# Revit family: Mailboxes_4C-Salsbury_Industries-Rear_Load-14_Door_High_Units
name_source: partatom
category: Specialty Equipment
revit_build: Autodesk Revit 2016 (Build: 20150714_1515(x64)
units: mm (PartAtom-declared; Revit-internal decimal feet)

## family parameters
Always vertical = Yes
Cut with Voids When Loaded = No
Host = Wall
OmniClass Number = 23.40.90.14.11
OmniClass Title = Mail Boxes
Part Type = Normal
Room Calculation Point = No
Round Connector Dimension = Use Diameter
Shared = No

## types (14) — shared parameters
Assembly Code = C1030910
Assembly Description = Mailboxes
Back Enclosure Material = Aluminum - Salsbury Finish - Anodized
Bottom Back Plate = No
Depth = 17.025"
Height = 51.500"
Latch Distance = 9.515"
Latch Locks-Right Side = Yes
Lock Material = Stainless Steel - Salsbury Finish -  Polished
Manufacturer = Salsbury Industries
MasterFormat Number = 10 55 00
MasterFormat Title = Postal Specialties
OmniClass 23 Number = 23.40.90.14.11
OmniClass 23 Title = Mail Boxes
Top Back Plate = No
URL = www.mailboxes.com
Version = 3.0 (06/30/17)

## per-type parameters (varying)
- 3714D-16 RL: Description=14 Door High Unit:  16 MB1, 2 PL5, OM2; Door Slot L1=3700 Series 4C Door Configurations : MB1 Door; Door Slot L10=3700 Series 4C Door Configurations : Empty; Door Slot L11=3700 Series 4C Door Configurations : Empty; Door Slot L12=3700 Series 4C Door Configurations : Empty; Door Slot L13=3700 Series 4C Door Configurations : Empty; Door Slot L14=3700 Series 4C Parcel Configurations : PL5 w/ Divider; Door Slot L2=3700 Series 4C Door Configurations : MB1 Door w/ Divider; Door Slot L3=3700 Series 4C Door Configurations : MB1 Door w/ Divider; Door Slot L4=3700 Series 4C Door Configurations : MB1 Door w/ Divider; Door Slot L5=3700 Series 4C Door Configurations : MB1 Door w/ Divider; Door Slot L6=3700 Series 4C Door Configurations : MB1 Door w/ Divider; Door Slot L7=3700 Series 4C Door Configurations : MB1 Door w/ Divider; Door Slot L8=3700 Series 4C Door Configurations : MB1 Door w/ Divider; Door Slot L9=3700 Series 4C Door Configurations : MB1 Door w/ Divider; Door Slot R1=3700 Series 4C Door Configurations : MB1 Door w/ Divider; Door Slot R10=3700 Series 4C Door Configurations : Empty; Door Slot R11=3700 Series 4C Door Configurations : Empty; Door Slot R12=3700 Series 4C Door Configurations : Empty; Door Slot R13=3700 Series 4C Door Configurations : Empty; Door Slot R14=3700 Series 4C Parcel Configurations : PL5 w/ Divider; Door Slot R2=3700 Series 4C Door Configurations : MB1 Door w/ Divider; Door Slot R3=3700 Series 4C Door Configurations : MB1 Door w/ Divider; Door Slot R4=3700 Series 4C Door Configurations : MB1 Door w/ Divider; Door Slot R5=3700 Series 4C Door Configurations : MB1 Door w/ Divider; Door Slot R6=3700 Series 4C Door Configurations : Empty; Door Slot R7=3700 Series 4C OM2 Configuration : OM2-RL; Door Slot R8=3700 Series 4C Door Configurations : MB1 Door w/ Divider; Door Slot R9=3700 Series 4C Door Configurations : MB1 Door w/ Divider; Latch Alignment=14.857"; Latch Locks-Left Side=Yes; Left Inside Wall=Yes; Right Inside Wall=Yes; Type Comments=4C Standard Horizontal Mailbox - Rear Loading; Vertical Center Divider=Yes; Width=31.098"
- 3714S-2B RL: Description=14 Door High Unit:- 2 Receptacle Bins; Door Slot L1=3700 Series 4C Door Configurations : Empty; Door Slot L10=3700 Series 4C Door Configurations : Empty; Door Slot L11=3700 Series 4C Door Configurations : Empty; Door Slot L12=3700 Series 4C Door Configurations : Empty; Door Slot L13=3700 Series 4C Door Configurations : Empty; Door Slot L14=3700 Series 4C Door Configurations : Empty; Door Slot L2=3700 Series 4C Door Configurations : Empty; Door Slot L3=3700 Series 4C Door Configurations : Empty; Door Slot L4=3700 Series 4C Door Configurations : Empty; Door Slot L5=3700 Series 4C Door Configurations : Empty; Door Slot L6=3700 Series 4C Door Configurations : Empty; Door Slot L7=3700 Series 4C Door Configurations : Empty; Door Slot L8=3700 Series 4C Door Configurations : Empty; Door Slot L9=3700 Series 4C Door Configurations : Empty; Door Slot R1=3700 Series 4C Door Configurations : Empty; Door Slot R10=3700 Series 4C Door Configurations : Empty; Door Slot R11=3700 Series 4C Door Configurations : Empty; Door Slot R12=3700 Series 4C Door Configurations : Empty; Door Slot R13=3700 Series 4C Door Configurations : Empty; Door Slot R14=4C-14 Door High Receptacle; Door Slot R2=3700 Series 4C Door Configurations : Empty; Door Slot R3=3700 Series 4C Door Configurations : Empty; Door Slot R4=3700 Series 4C Door Configurations : Empty; Door Slot R5=3700 Series 4C Door Configurations : Empty; Door Slot R6=3700 Series 4C Door Configurations : Empty; Door Slot R7=3700 Series 4C Door Configurations : Empty; Door Slot R8=3700 Series 4C Door Configurations : Empty; Door Slot R9=3700 Series 4C Door Configurations : Empty; Latch Alignment=13.876"; Latch Locks-Left Side=No; Left Inside Wall=No; Right Inside Wall=No; Type Comments=4C Horizontal Receptacle Bin - Rear Loading; Vertical Center Divider=No; Width=16.344"
- 3714S-07 RL: Description=14 Door High Unit:  7 MB1, 1 PL5, OM2; Door Slot L1=3700 Series 4C Door Configurations : Empty; Door Slot L10=3700 Series 4C Door Configurations : Empty; Door Slot L11=3700 Series 4C Door Configurations : Empty; Door Slot L12=3700 Series 4C Door Configurations : Empty; Door Slot L13=3700 Series 4C Door Configurations : Empty; Door Slot L14=3700 Series 4C Door Configurations : Empty; Door Slot L2=3700 Series 4C Door Configurations : Empty; Door Slot L3=3700 Series 4C Door Configurations : Empty; Door Slot L4=3700 Series 4C Door Configurations : Empty; Door Slot L5=3700 Series 4C Door Configurations : Empty; Door Slot L6=3700 Series 4C Door Configurations : Empty; Door Slot L7=3700 Series 4C Door Configurations : Empty; Door Slot L8=3700 Series 4C Door Configurations : Empty; Door Slot L9=3700 Series 4C Door Configurations : Empty; Door Slot R1=3700 Series 4C Door Configurations : MB1 Door; Door Slot R10=3700 Series 4C Door Configurations : Empty; Door Slot R11=3700 Series 4C Door Configurations : Empty; Door Slot R12=3700 Series 4C Door Configurations : Empty; Door Slot R13=3700 Series 4C Door Configurations : Empty; Door Slot R14=3700 Series 4C Parcel Configurations : PL5 w/ Divider; Door Slot R2=3700 Series 4C Door Configurations : MB1 Door w/ Divider; Door Slot R3=3700 Series 4C Door Configurations : MB1 Door w/ Divider; Door Slot R4=3700 Series 4C Door Configurations : MB1 Door w/ Divider; Door Slot R5=3700 Series 4C Door Configurations : MB1 Door w/ Divider; Door Slot R6=3700 Series 4C Door Configurations : Empty; Door Slot R7=3700 Series 4C OM2 Configuration : OM2-RL; Door Slot R8=3700 Series 4C Door Configurations : MB1 Door w/ Divider; Door Slot R9=3700 Series 4C Door Configurations : MB1 Door w/ Divider; Latch Alignment=13.876"; Latch Locks-Left Side=No; Left Inside Wall=No; Right Inside Wall=No; Type Comments=4C Standard Horizontal Mailbox - Rear Loading; Vertical Center Divider=No; Width=16.344"
- 3714S-1C RL: Description=14 Door High Unit; Door Slot L1=3700 Series 4C Door Configurations : Empty; Door Slot L10=3700 Series 4C Door Configurations : Empty; Door Slot L11=3700 Series 4C Door Configurations : Empty; Door Slot L12=3700 Series 4C Door Configurations : Empty; Door Slot L13=3700 Series 4C Door Configurations : Empty; Door Slot L14=3700 Series 4C Door Configurations : Empty; Door Slot L2=3700 Series 4C Door Configurations : Empty; Door Slot L3=3700 Series 4C Door Configurations : Empty; Door Slot L4=3700 Series 4C Door Configurations : Empty; Door Slot L5=3700 Series 4C Door Configurations : Empty; Door Slot L6=3700 Series 4C Door Configurations : Empty; Door Slot L7=3700 Series 4C Door Configurations : Empty; Door Slot L8=3700 Series 4C Door Configurations : Empty; Door Slot L9=3700 Series 4C Door Configurations : Empty; Door Slot R1=3700 Series 4C Door Configurations : Empty; Door Slot R10=3700 Series 4C Door Configurations : Empty; Door Slot R11=3700 Series 4C Door Configurations : Empty; Door Slot R12=3700 Series 4C Door Configurations : Empty; Door Slot R13=3700 Series 4C Door Configurations : Empty; Door Slot R14=4C-14 Door High Collection Box; Door Slot R2=3700 Series 4C Door Configurations : Empty; Door Slot R3=3700 Series 4C Door Configurations : Empty; Door Slot R4=3700 Series 4C Door Configurations : Empty; Door Slot R5=3700 Series 4C Door Configurations : Empty; Door Slot R6=3700 Series 4C Door Configurations : Empty; Door Slot R7=3700 Series 4C Door Configurations : Empty; Door Slot R8=3700 Series 4C Door Configurations : Empty; Door Slot R9=3700 Series 4C Door Configurations : Empty; Latch Alignment=13.876"; Latch Locks-Left Side=No; Left Inside Wall=No; Right Inside Wall=No; Type Comments=4C Horizontal Collection Box - Rear Loading; Vertical Center Divider=No; Width=16.344"
- 3714D-15 RL: Description=14 Door High Unit:  15 MB1, 1 PL5, 1 PL6, OM2; Door Slot L1=3700 Series 4C Door Configurations : MB1 Door; Door Slot L10=3700 Series 4C Door Configurations : Empty; Door Slot L11=3700 Series 4C Door Configurations : Empty; Door Slot L12=3700 Series 4C Door Configurations : Empty; Door Slot L13=3700 Series 4C Door Configurations : Empty; Door Slot L14=3700 Series 4C Parcel Configurations : PL6 w/ Divider; Door Slot L2=3700 Series 4C Door Configurations : MB1 Door w/ Divider; Door Slot L3=3700 Series 4C Door Configurations : MB1 Door w/ Divider; Door Slot L4=3700 Series 4C Door Configurations : MB1 Door w/ Divider; Door Slot L5=3700 Series 4C Door Configurations : MB1 Door w/ Divider; Door Slot L6=3700 Series 4C Door Configurations : MB1 Door w/ Divider; Door Slot L7=3700 Series 4C Door Configurations : MB1 Door w/ Divider; Door Slot L8=3700 Series 4C Door Configurations : MB1 Door w/ Divider; Door Slot L9=3700 Series 4C Door Configurations : Empty; Door Slot R1=3700 Series 4C Door Configurations : MB1 Door w/ Divider; Door Slot R10=3700 Series 4C Door Configurations : Empty; Door Slot R11=3700 Series 4C Door Configurations : Empty; Door Slot R12=3700 Series 4C Door Configurations : Empty; Door Slot R13=3700 Series 4C Door Configurations : Empty; Door Slot R14=3700 Series 4C Parcel Configurations : PL5 w/ Divider; Door Slot R2=3700 Series 4C Door Configurations : MB1 Door w/ Divider; Door Slot R3=3700 Series 4C Door Configurations : MB1 Door w/ Divider; Door Slot R4=3700 Series 4C Door Configurations : MB1 Door w/ Divider; Door Slot R5=3700 Series 4C Door Configurations : MB1 Door w/ Divider; Door Slot R6=3700 Series 4C Door Configurations : Empty; Door Slot R7=3700 Series 4C OM2 Configuration : OM2-RL; Door Slot R8=3700 Series 4C Door Configurations : MB1 Door w/ Divider; Door Slot R9=3700 Series 4C Door Configurations : MB1 Door w/ Divider; Latch Alignment=14.857"; Latch Locks-Left Side=Yes; Left Inside Wall=Yes; Right Inside Wall=Yes; Type Comments=4C Standard Horizontal Mailbox - Rear Loading; Vertical Center Divider=Yes; Width=31.098"
- 3714D-14 RL: Description=14 Door High Unit:  14 MB1, 2 PL6, OM2; Door Slot L1=3700 Series 4C Door Configurations : MB1 Door; Door Slot L10=3700 Series 4C Door Configurations : Empty; Door Slot L11=3700 Series 4C Door Configurations : Empty; Door Slot L12=3700 Series 4C Door Configurations : Empty; Door Slot L13=3700 Series 4C Door Configurations : Empty; Door Slot L14=3700 Series 4C Parcel Configurations : PL6 w/ Divider; Door Slot L2=3700 Series 4C Door Configurations : MB1 Door w/ Divider; Door Slot L3=3700 Series 4C Door Configurations : MB1 Door w/ Divider; Door Slot L4=3700 Series 4C Door Configurations : MB1 Door w/ Divider; Door Slot L5=3700 Series 4C Door Configurations : MB1 Door w/ Divider; Door Slot L6=3700 Series 4C Door Configurations : MB1 Door w/ Divider; Door Slot L7=3700 Series 4C Door Configurations : MB1 Door w/ Divider; Door Slot L8=3700 Series 4C Door Configurations : MB1 Door w/ Divider; Door Slot L9=3700 Series 4C Door Configurations : Empty; Door Slot R1=3700 Series 4C Door Configurations : MB1 Door w/ Divider; Door Slot R10=3700 Series 4C Door Configurations : Empty; Door Slot R11=3700 Series 4C Door Configurations : Empty; Door Slot R12=3700 Series 4C Door Configurations : Empty; Door Slot R13=3700 Series 4C Door Configurations : Empty; Door Slot R14=3700 Series 4C Parcel Configurations : PL6 w/ Divider; Door Slot R2=3700 Series 4C Door Configurations : MB1 Door w/ Divider; Door Slot R3=3700 Series 4C Door Configurations : MB1 Door w/ Divider; Door Slot R4=3700 Series 4C Door Configurations : MB1 Door w/ Divider; Door Slot R5=3700 Series 4C Door Configurations : MB1 Door w/ Divider; Door Slot R6=3700 Series 4C Door Configurations : Empty; Door Slot R7=3700 Series 4C OM2 Configuration : OM2-RL; Door Slot R8=3700 Series 4C Door Configurations : MB1 Door w/ Divider; Door Slot R9=3700 Series 4C Door Configurations : Empty; Latch Alignment=14.857"; Latch Locks-Left Side=Yes; Left Inside Wall=Yes; Right Inside Wall=Yes; Type Comments=4C Standard Horizontal Mailbox - Rear Loading; Vertical Center Divider=Yes; Width=31.098"
- 3714D-07 RL: Description=14 Door High Unit:  7 MB2, 2 PL6, OM2; Door Slot L1=3700 Series 4C Door Configurations : Empty; Door Slot L10=3700 Series 4C Door Configurations : Empty; Door Slot L11=3700 Series 4C Door Configurations : Empty; Door Slot L12=3700 Series 4C Door Configurations : Empty; Door Slot L13=3700 Series 4C Door Configurations : Empty; Door Slot L14=3700 Series 4C Parcel Configurations : PL6 w/ Divider; Door Slot L2=3700 Series 4C Door Configurations : MB2 Door; Door Slot L3=3700 Series 4C Door Configurations : Empty; Door Slot L4=3700 Series 4C Door Configurations : MB2 Door w/ Divider; Door Slot L5=3700 Series 4C Door Configurations : Empty; Door Slot L6=3700 Series 4C Door Configurations : MB2 Door w/ Divider; Door Slot L7=3700 Series 4C Door Configurations : Empty; Door Slot L8=3700 Series 4C Door Configurations : MB2 Door w/ Divider; Door Slot L9=3700 Series 4C Door Configurations : Empty; Door Slot R1=3700 Series 4C Door Configurations : Empty; Door Slot R10=3700 Series 4C Door Configurations : Empty; Door Slot R11=3700 Series 4C Door Configurations : Empty; Door Slot R12=3700 Series 4C Door Configurations : Empty; Door Slot R13=3700 Series 4C Door Configurations : Empty; Door Slot R14=3700 Series 4C Parcel Configurations : PL6 w/ Divider; Door Slot R2=3700 Series 4C Door Configurations : MB2 Door; Door Slot R3=3700 Series 4C Door Configurations : Empty; Door Slot R4=3700 Series 4C Door Configurations : MB2 Door w/ Divider; Door Slot R5=3700 Series 4C Door Configurations : Empty; Door Slot R6=3700 Series 4C Door Configurations : MB2 Door w/ Divider; Door Slot R7=3700 Series 4C Door Configurations : Empty; Door Slot R8=3700 Series 4C OM2 Configuration : OM2-RL; Door Slot R9=3700 Series 4C Door Configurations : Empty; Latch Alignment=14.857"; Latch Locks-Left Side=Yes; Left Inside Wall=Yes; Right Inside Wall=Yes; Type Comments=4C Standard Horizontal Mailbox - Rear Loading; Vertical Center Divider=Yes; Width=31.098"
- 3714D-13 RL: Description=14 Door High Unit:  13 MB2, OM2; Door Slot L1=3700 Series 4C Door Configurations : Empty; Door Slot L10=3700 Series 4C Door Configurations : MB2 Door w/ Divider; Door Slot L11=3700 Series 4C Door Configurations : Empty; Door Slot L12=3700 Series 4C Door Configurations : MB2 Door w/ Divider; Door Slot L13=3700 Series 4C Door Configurations : Empty; Door Slot L14=3700 Series 4C Door Configurations : MB2 Door w/ Divider; Door Slot L2=3700 Series 4C Door Configurations : MB2 Door; Door Slot L3=3700 Series 4C Door Configurations : Empty; Door Slot L4=3700 Series 4C Door Configurations : MB2 Door w/ Divider; Door Slot L5=3700 Series 4C Door Configurations : Empty; Door Slot L6=3700 Series 4C Door Configurations : MB2 Door w/ Divider; Door Slot L7=3700 Series 4C Door Configurations : Empty; Door Slot L8=3700 Series 4C Door Configurations : MB2 Door w/ Divider; Door Slot L9=3700 Series 4C Door Configurations : Empty; Door Slot R1=3700 Series 4C Door Configurations : Empty; Door Slot R10=3700 Series 4C Door Configurations : MB2 Door w/ Divider; Door Slot R11=3700 Series 4C Door Configurations : Empty; Door Slot R12=3700 Series 4C Door Configurations : MB2 Door w/ Divider; Door Slot R13=3700 Series 4C Door Configurations : Empty; Door Slot R14=3700 Series 4C Door Configurations : MB2 Door w/ Divider; Door Slot R2=3700 Series 4C Door Configurations : MB2 Door; Door Slot R3=3700 Series 4C Door Configurations : Empty; Door Slot R4=3700 Series 4C Door Configurations : MB2 Door w/ Divider; Door Slot R5=3700 Series 4C Door Configurations : Empty; Door Slot R6=3700 Series 4C Door Configurations : MB2 Door w/ Divider; Door Slot R7=3700 Series 4C Door Configurations : Empty; Door Slot R8=3700 Series 4C OM2 Configuration : OM2-RL; Door Slot R9=3700 Series 4C Door Configurations : Empty; Latch Alignment=14.857"; Latch Locks-Left Side=Yes; Left Inside Wall=Yes; Right Inside Wall=Yes; Type Comments=4C Standard Horizontal Mailbox - Rear Loading; Vertical Center Divider=Yes; Width=31.098"
- 3714D-26 RL: Description=14 Door High Unit:  26 MB2, OM2; Door Slot L1=3700 Series 4C Door Configurations : MB1 Door; Door Slot L10=3700 Series 4C Door Configurations : MB1 Door w/ Divider; Door Slot L11=3700 Series 4C Door Configurations : MB1 Door w/ Divider; Door Slot L12=3700 Series 4C Door Configurations : MB1 Door w/ Divider; Door Slot L13=3700 Series 4C Door Configurations : MB1 Door w/ Divider; Door Slot L14=3700 Series 4C Door Configurations : MB1 Door w/ Divider; Door Slot L2=3700 Series 4C Door Configurations : MB1 Door w/ Divider; Door Slot L3=3700 Series 4C Door Configurations : MB1 Door w/ Divider; Door Slot L4=3700 Series 4C Door Configurations : MB1 Door w/ Divider; Door Slot L5=3700 Series 4C Door Configurations : MB1 Door w/ Divider; Door Slot L6=3700 Series 4C Door Configurations : MB1 Door w/ Divider; Door Slot L7=3700 Series 4C Door Configurations : MB1 Door w/ Divider; Door Slot L8=3700 Series 4C Door Configurations : MB1 Door w/ Divider; Door Slot L9=3700 Series 4C Door Configurations : MB1 Door w/ Divider; Door Slot R1=3700 Series 4C Door Configurations : MB1 Door; Door Slot R10=3700 Series 4C Door Configurations : MB1 Door w/ Divider; Door Slot R11=3700 Series 4C Door Configurations : MB1 Door w/ Divider; Door Slot R12=3700 Series 4C Door Configurations : MB1 Door w/ Divider; Door Slot R13=3700 Series 4C Door Configurations : MB1 Door w/ Divider; Door Slot R14=3700 Series 4C Door Configurations : MB1 Door w/ Divider; Door Slot R2=3700 Series 4C Door Configurations : MB1 Door w/ Divider; Door Slot R3=3700 Series 4C Door Configurations : MB1 Door w/ Divider; Door Slot R4=3700 Series 4C Door Configurations : MB1 Door w/ Divider; Door Slot R5=3700 Series 4C Door Configurations : MB1 Door w/ Divider; Door Slot R6=3700 Series 4C Door Configurations : MB1 Door w/ Divider; Door Slot R7=3700 Series 4C Door Configurations : Empty; Door Slot R8=3700 Series 4C OM2 Configuration : OM2-RL; Door Slot R9=3700 Series 4C Door Configurations : MB1 Door w/ Divider; Latch Alignment=14.857"; Latch Locks-Left Side=Yes; Left Inside Wall=Yes; Right Inside Wall=Yes; Type Comments=4C Standard Horizontal Mailbox - Rear Loading; Vertical Center Divider=Yes; Width=31.098"
- 3714S-03 RL: Description=14 Door High Unit:  3 MB2, 1 PL6, OM2; Door Slot L1=3700 Series 4C Door Configurations : Empty; Door Slot L10=3700 Series 4C Door Configurations : Empty; Door Slot L11=3700 Series 4C Door Configurations : Empty; Door Slot L12=3700 Series 4C Door Configurations : Empty; Door Slot L13=3700 Series 4C Door Configurations : Empty; Door Slot L14=3700 Series 4C Door Configurations : Empty; Door Slot L2=3700 Series 4C Door Configurations : Empty; Door Slot L3=3700 Series 4C Door Configurations : Empty; Door Slot L4=3700 Series 4C Door Configurations : Empty; Door Slot L5=3700 Series 4C Door Configurations : Empty; Door Slot L6=3700 Series 4C Door Configurations : Empty; Door Slot L7=3700 Series 4C Door Configurations : Empty; Door Slot L8=3700 Series 4C Door Configurations : Empty; Door Slot L9=3700 Series 4C Door Configurations : Empty; Door Slot R1=3700 Series 4C Door Configurations : Empty; Door Slot R10=3700 Series 4C Door Configurations : Empty; Door Slot R11=3700 Series 4C Door Configurations : Empty; Door Slot R12=3700 Series 4C Door Configurations : Empty; Door Slot R13=3700 Series 4C Door Configurations : Empty; Door Slot R14=3700 Series 4C Parcel Configurations : PL6 w/ Divider; Door Slot R2=3700 Series 4C Door Configurations : MB2 Door; Door Slot R3=3700 Series 4C Door Configurations : Empty; Door Slot R4=3700 Series 4C Door Configurations : MB2 Door w/ Divider; Door Slot R5=3700 Series 4C Door Configurations : Empty; Door Slot R6=3700 Series 4C Door Configurations : MB2 Door w/ Divider; Door Slot R7=3700 Series 4C Door Configurations : Empty; Door Slot R8=3700 Series 4C OM2 Configuration : OM2-RL; Door Slot R9=3700 Series 4C Door Configurations : Empty; Latch Alignment=13.876"; Latch Locks-Left Side=No; Left Inside Wall=No; Right Inside Wall=No; Type Comments=4C Standard Horizontal Mailbox - Rear Loading; Vertical Center Divider=No; Width=16.344"
- 3714S-2P RL: Description=14 Door High Unit:  2 PL6, OM2; Door Slot L1=3700 Series 4C Door Configurations : Empty; Door Slot L10=3700 Series 4C Door Configurations : Empty; Door Slot L11=3700 Series 4C Door Configurations : Empty; Door Slot L12=3700 Series 4C Door Configurations : Empty; Door Slot L13=3700 Series 4C Door Configurations : Empty; Door Slot L14=3700 Series 4C Door Configurations : Empty; Door Slot L2=3700 Series 4C Door Configurations : Empty; Door Slot L3=3700 Series 4C Door Configurations : Empty; Door Slot L4=3700 Series 4C Door Configurations : Empty; Door Slot L5=3700 Series 4C Door Configurations : Empty; Door Slot L6=3700 Series 4C Door Configurations : Empty; Door Slot L7=3700 Series 4C Door Configurations : Empty; Door Slot L8=3700 Series 4C Door Configurations : Empty; Door Slot L9=3700 Series 4C Door Configurations : Empty; Door Slot R1=3700 Series 4C Door Configurations : Empty; Door Slot R10=3700 Series 4C Door Configurations : Empty; Door Slot R11=3700 Series 4C Door Configurations : Empty; Door Slot R12=3700 Series 4C Door Configurations : Empty; Door Slot R13=3700 Series 4C Door Configurations : Empty; Door Slot R14=3700 Series 4C Parcel Configurations : PL6 w/ Divider; Door Slot R2=3700 Series 4C Door Configurations : Empty; Door Slot R3=3700 Series 4C Door Configurations : Empty; Door Slot R4=3700 Series 4C Door Configurations : Empty; Door Slot R5=3700 Series 4C Door Configurations : Empty; Door Slot R6=3700 Series 4C Parcel Configurations : PL6; Door Slot R7=3700 Series 4C Door Configurations : Empty; Door Slot R8=3700 Series 4C OM2 Configuration : OM2-RL; Door Slot R9=3700 Series 4C Door Configurations : Empty; Latch Alignment=13.876"; Latch Locks-Left Side=No; Left Inside Wall=No; Right Inside Wall=No; Type Comments=4C Standard Horizontal Mailbox - Rear Loading; Vertical Center Divider=No; Width=16.344"
- 3714S-3P RL: Description=14 Door High Unit:  1 PL4, 2 PL5; Door Slot L1=3700 Series 4C Door Configurations : Empty; Door Slot L10=3700 Series 4C Door Configurations : Empty; Door Slot L11=3700 Series 4C Door Configurations : Empty; Door Slot L12=3700 Series 4C Door Configurations : Empty; Door Slot L13=3700 Series 4C Door Configurations : Empty; Door Slot L14=3700 Series 4C Door Configurations : Empty; Door Slot L2=3700 Series 4C Door Configurations : Empty; Door Slot L3=3700 Series 4C Door Configurations : Empty; Door Slot L4=3700 Series 4C Door Configurations : Empty; Door Slot L5=3700 Series 4C Door Configurations : Empty; Door Slot L6=3700 Series 4C Door Configurations : Empty; Door Slot L7=3700 Series 4C Door Configurations : Empty; Door Slot L8=3700 Series 4C Door Configurations : Empty; Door Slot L9=3700 Series 4C Door Configurations : Empty; Door Slot R1=3700 Series 4C Door Configurations : Empty; Door Slot R10=3700 Series 4C Door Configurations : Empty; Door Slot R11=3700 Series 4C Door Configurations : Empty; Door Slot R12=3700 Series 4C Door Configurations : Empty; Door Slot R13=3700 Series 4C Door Configurations : Empty; Door Slot R14=3700 Series 4C Parcel Configurations : PL5 w/ Divider; Door Slot R2=3700 Series 4C Door Configurations : Empty; Door Slot R3=3700 Series 4C Door Configurations : Empty; Door Slot R4=3700 Series 4C Parcel Configurations : PL4; Door Slot R5=3700 Series 4C Door Configurations : Empty; Door Slot R6=3700 Series 4C Door Configurations : Empty; Door Slot R7=3700 Series 4C Door Configurations : Empty; Door Slot R8=3700 Series 4C Door Configurations : Empty; Door Slot R9=3700 Series 4C Parcel Configurations : PL5 w/ Divider; Latch Alignment=13.876"; Latch Locks-Left Side=No; Left Inside Wall=No; Right Inside Wall=No; Type Comments=4C Standard Horizontal Mailbox - Rear Loading; Vertical Center Divider=No; Width=16.344"
- 3714S-12 RL: Description=14 Door High Unit:  12 MB1, OM2; Door Slot L1=3700 Series 4C Door Configurations : Empty; Door Slot L10=3700 Series 4C Door Configurations : Empty; Door Slot L11=3700 Series 4C Door Configurations : Empty; Door Slot L12=3700 Series 4C Door Configurations : Empty; Door Slot L13=3700 Series 4C Door Configurations : Empty; Door Slot L14=3700 Series 4C Door Configurations : Empty; Door Slot L2=3700 Series 4C Door Configurations : Empty; Door Slot L3=3700 Series 4C Door Configurations : Empty; Door Slot L4=3700 Series 4C Door Configurations : Empty; Door Slot L5=3700 Series 4C Door Configurations : Empty; Door Slot L6=3700 Series 4C Door Configurations : Empty; Door Slot L7=3700 Series 4C Door Configurations : Empty; Door Slot L8=3700 Series 4C Door Configurations : Empty; Door Slot L9=3700 Series 4C Door Configurations : Empty; Door Slot R1=3700 Series 4C Door Configurations : MB1 Door; Door Slot R10=3700 Series 4C Door Configurations : MB1 Door w/ Divider; Door Slot R11=3700 Series 4C Door Configurations : MB1 Door w/ Divider; Door Slot R12=3700 Series 4C Door Configurations : MB1 Door w/ Divider; Door Slot R13=3700 Series 4C Door Configurations : MB1 Door w/ Divider; Door Slot R14=3700 Series 4C Door Configurations : MB1 Door w/ Divider; Door Slot R2=3700 Series 4C Door Configurations : MB1 Door w/ Divider; Door Slot R3=3700 Series 4C Door Configurations : MB1 Door w/ Divider; Door Slot R4=3700 Series 4C Door Configurations : MB1 Door w/ Divider; Door Slot R5=3700 Series 4C Door Configurations : MB1 Door w/ Divider; Door Slot R6=3700 Series 4C Door Configurations : MB1 Door w/ Divider; Door Slot R7=3700 Series 4C Door Configurations : Empty; Door Slot R8=3700 Series 4C OM2 Configuration : OM2-RL; Door Slot R9=3700 Series 4C Door Configurations : MB1 Door w/ Divider; Latch Alignment=13.876"; Latch Locks-Left Side=No; Left Inside Wall=No; Right Inside Wall=No; Type Comments=4C Standard Horizontal Mailbox - Rear Loading; Vertical Center Divider=No; Width=16.344"
- 3714S-06 RL: Description=14 Door High Unit:  6 MB2, OM2; Door Slot L1=3700 Series 4C Door Configurations : Empty; Door Slot L10=3700 Series 4C Door Configurations : Empty; Door Slot L11=3700 Series 4C Door Configurations : Empty; Door Slot L12=3700 Series 4C Door Configurations : Empty; Door Slot L13=3700 Series 4C Door Configurations : Empty; Door Slot L14=3700 Series 4C Door Configurations : Empty; Door Slot L2=3700 Series 4C Door Configurations : Empty; Door Slot L3=3700 Series 4C Door Configurations : Empty; Door Slot L4=3700 Series 4C Door Configurations : Empty; Door Slot L5=3700 Series 4C Door Configurations : Empty; Door Slot L6=3700 Series 4C Door Configurations : Empty; Door Slot L7=3700 Series 4C Door Configurations : Empty; Door Slot L8=3700 Series 4C Door Configurations : Empty; Door Slot L9=3700 Series 4C Door Configurations : Empty; Door Slot R1=3700 Series 4C Door Configurations : Empty; Door Slot R10=3700 Series 4C Door Configurations : MB2 Door w/ Divider; Door Slot R11=3700 Series 4C Door Configurations : Empty; Door Slot R12=3700 Series 4C Door Configurations : MB2 Door w/ Divider; Door Slot R13=3700 Series 4C Door Configurations : Empty; Door Slot R14=3700 Series 4C Door Configurations : MB2 Door w/ Divider; Door Slot R2=3700 Series 4C Door Configurations : MB2 Door; Door Slot R3=3700 Series 4C Door Configurations : Empty; Door Slot R4=3700 Series 4C Door Configurations : MB2 Door w/ Divider; Door Slot R5=3700 Series 4C Door Configurations : Empty; Door Slot R6=3700 Series 4C Door Configurations : MB2 Door w/ Divider; Door Slot R7=3700 Series 4C Door Configurations : Empty; Door Slot R8=3700 Series 4C OM2 Configuration : OM2-RL; Door Slot R9=3700 Series 4C Door Configurations : Empty; Latch Alignment=13.876"; Latch Locks-Left Side=No; Left Inside Wall=No; Right Inside Wall=No; Type Comments=4C Standard Horizontal Mailbox - Rear Loading; Vertical Center Divider=No; Width=16.344"

note: column(s) folded — value = type name in every type: Model

## geometry (parser evidence)
native form markers: Blend x2, Sweep x24
no freeform markers — native parametric forms only
